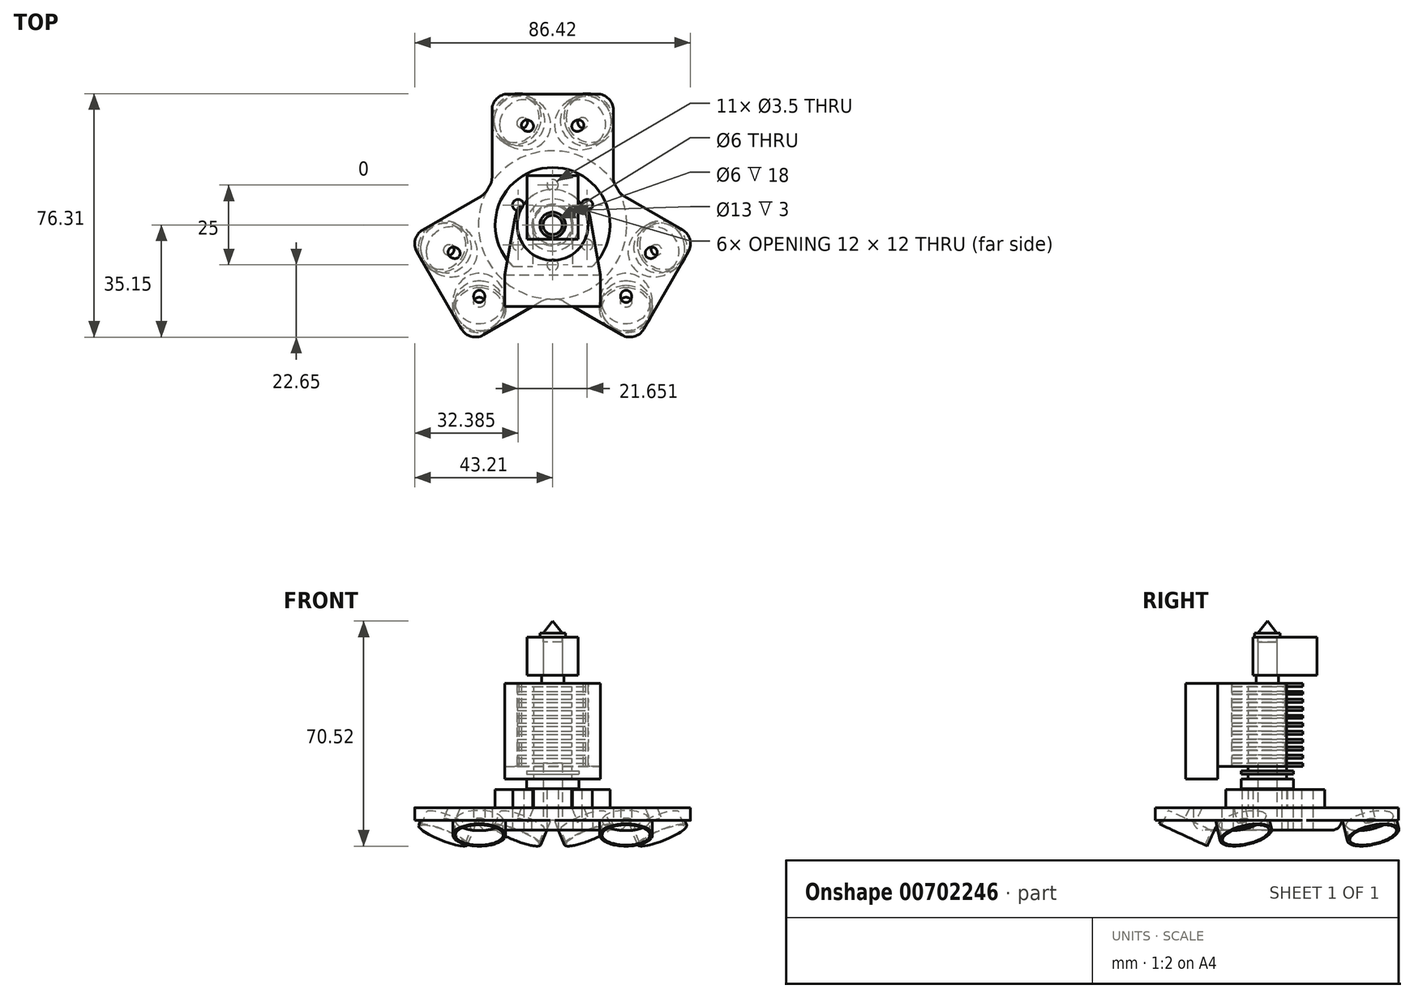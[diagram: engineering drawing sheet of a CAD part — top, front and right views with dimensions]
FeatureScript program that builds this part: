
annotation { "Feature Type Name" : "Feature", "Feature Type Description" : "" }
export const myFeature = defineFeature(function(context is Context, id is Id, definition is map)
    precondition{}
    {
        {
            var Q0;
            Q0=qCreatedBy(makeId("Top.planeOp"),FACE);
            var sketch = newSketch(context, id + "F0", { "sketchPlane" : qUnion([Q0])});
            skLineSegment(sketch, "E0", {"start": v(35.54, -20.52) * mm, "end": v(-20.14, 11.63) * mm, "construction": true});
            skLineSegment(sketch, "E1", {"start": v(0, 41.04) * mm, "end": v(0, -23.25) * mm, "construction": true});
            skLineSegment(sketch, "E2", {"start": v(-33.07, -19.1) * mm, "end": v(20.14, 11.62) * mm, "construction": true});
            skPoint(sketch, "E3", {"position": v(0, 0) * mm});
            skCircle(sketch, "E4", {"center": v(0, 0) * mm, "radius": 23.25 * mm});
            skPoint(sketch, "E5.visualSharp", {"position": v(-19, 41.04) * mm});
            skPoint(sketch, "E6.visualSharp", {"position": v(19, 41.04) * mm});
            skPoint(sketch, "E7.visualSharp", {"position": v(45.04, -4.07) * mm});
            skPoint(sketch, "E8.visualSharp", {"position": v(26.04, -36.98) * mm});
            skPoint(sketch, "E9.visualSharp", {"position": v(-26.04, -36.98) * mm});
            skPoint(sketch, "E10.visualSharp", {"position": v(-45.04, -4.07) * mm});
            skCircle(sketch, "E11", {"center": v(0, 0) * mm, "radius": 8 * mm});
            skCircle(sketch, "E12", {"center": v(0, 12.5) * mm, "radius": 1.75 * mm});
            skCircle(sketch, "E13", {"center": v(10.83, 6.25) * mm, "radius": 1.75 * mm});
            skCircle(sketch, "E14", {"center": v(10.83, -6.25) * mm, "radius": 1.75 * mm});
            skCircle(sketch, "E15", {"center": v(0, -12.5) * mm, "radius": 1.75 * mm});
            skCircle(sketch, "E16", {"center": v(-10.83, -6.25) * mm, "radius": 1.75 * mm});
            skCircle(sketch, "E17", {"center": v(-10.83, 6.25) * mm, "radius": 1.75 * mm});
            skCircle(sketch, "E18", {"center": v(0, 0) * mm, "radius": 6.5 * mm});
            skPoint(sketch, "E19.orphan", {"position": v(-21.1, 9.75) * mm});
            skPoint(sketch, "E20.orphan", {"position": v(-19, 13.4) * mm});
            skPoint(sketch, "E21.orphan", {"position": v(19, 13.4) * mm});
            skPoint(sketch, "E22.orphan", {"position": v(21.1, 9.75) * mm});
            skPoint(sketch, "E23.orphan", {"position": v(-2.1, -23.15) * mm});
            skPoint(sketch, "E24.orphan", {"position": v(2.1, -23.15) * mm});
            skLineSegment(sketch, "E25", {"start": v(32.5, -7.8) * mm, "end": v(23, -24.25) * mm, "construction": true});
            skLineSegment(sketch, "E26", {"start": v(-23, -24.25) * mm, "end": v(-32.5, -7.8) * mm, "construction": true});
            skLineSegment(sketch, "E27", {"start": v(-9.5, 32.04) * mm, "end": v(9.5, 32.04) * mm, "construction": true});
            skLineSegment(sketch, "E28", {"start": v(23, -24.25) * mm, "end": v(-23, -24.25) * mm, "construction": true});
            skCircle(sketch, "E29", {"center": v(0, 0) * mm, "radius": 12.5 * mm});
            skLineSegment(sketch, "E30", {"start": v(19, 41.04) * mm, "end": v(19, 13.4) * mm});
            skLineSegment(sketch, "E31", {"start": v(-19, 41.04) * mm, "end": v(-19, 13.4) * mm});
            skLineSegment(sketch, "E32", {"start": v(-21.1, 9.75) * mm, "end": v(-45.04, -4.07) * mm});
            skLineSegment(sketch, "E33", {"start": v(-2.1, -23.15) * mm, "end": v(-26.04, -36.98) * mm});
            skLineSegment(sketch, "E34", {"start": v(2.1, -23.15) * mm, "end": v(26.04, -36.98) * mm});
            skLineSegment(sketch, "E35", {"start": v(45.04, -4.07) * mm, "end": v(21.1, 9.75) * mm});
            skLineSegment(sketch, "E36", {"start": v(45.04, -4.07) * mm, "end": v(26.04, -36.98) * mm});
            skLineSegment(sketch, "E37", {"start": v(-26.04, -36.98) * mm, "end": v(-45.04, -4.07) * mm});
            skLineSegment(sketch, "E38", {"start": v(19, 41.04) * mm, "end": v(-19, 41.04) * mm});
            skLineSegment(sketch, "E39", {"start": v(-9.5, 32.04) * mm, "end": v(-32.5, -7.8) * mm, "construction": true});
            skLineSegment(sketch, "E40", {"start": v(9.5, 32.04) * mm, "end": v(32.5, -7.8) * mm, "construction": true});
            skSolve(sketch);
        }
        {
            var Q0;
            {var subQ0=sQuery(id+"F0.wireOp",EDGE,"E4");var subQ1=sQuery(id+"F0.wireOp",EDGE,"E0");var subQ2=makeQuery(id+"F0.imprint","INTERSECT",VERTEX,{"disambiguationData":[OD(0.0)],"derivedFrom":[subQ1,subQ0]});Q0=makeQuery(id+"F0.imprint","IMPRINT",FACE,{"disambiguationData":[TD([[makeQuery(id+"F0.imprint","IMPRINT",EDGE,{"disambiguationData":[TD([[subQ2,1.0]])],"derivedFrom":subQ1}),-1.0]])]});}
            var Q1;
            {var subQ0=sQuery(id+"F0.wireOp",EDGE,"E4");var subQ6=sQuery(id+"F0.wireOp",EDGE,"E1");var subQ7=makeQuery(id+"F0.imprint","INTERSECT",VERTEX,{"disambiguationData":[OD(1.0)],"derivedFrom":[subQ6,subQ0]});Q1=makeQuery(id+"F0.imprint","IMPRINT",FACE,{"disambiguationData":[TD([[makeQuery(id+"F0.imprint","IMPRINT",EDGE,{"disambiguationData":[TD([[subQ7,-1.0]])],"derivedFrom":subQ6}),1.0]])]});}
            var Q2;
            {var subQ0=sQuery(id+"F0.wireOp",EDGE,"E4");var subQ4=sQuery(id+"F0.wireOp",EDGE,"E0");var subQ5=makeQuery(id+"F0.imprint","INTERSECT",VERTEX,{"disambiguationData":[OD(1.0)],"derivedFrom":[subQ4,subQ0]});Q2=makeQuery(id+"F0.imprint","IMPRINT",FACE,{"disambiguationData":[TD([[makeQuery(id+"F0.imprint","IMPRINT",EDGE,{"disambiguationData":[TD([[subQ5,-1.0]])],"derivedFrom":subQ4}),1.0]])]});}
            var Q3;
            {var subQ0=sQuery(id+"F0.wireOp",EDGE,"E4");var subQ1=sQuery(id+"F0.wireOp",EDGE,"E1");var subQ2=makeQuery(id+"F0.imprint","INTERSECT",VERTEX,{"disambiguationData":[OD(0.0)],"derivedFrom":[subQ1,subQ0]});Q3=makeQuery(id+"F0.imprint","IMPRINT",FACE,{"disambiguationData":[TD([[makeQuery(id+"F0.imprint","IMPRINT",EDGE,{"disambiguationData":[TD([[subQ2,1.0]])],"derivedFrom":subQ1}),-1.0]])]});}
            var Q4;
            {var subQ0=sQuery(id+"F0.wireOp",EDGE,"E4");var subQ6=sQuery(id+"F0.wireOp",EDGE,"E0");var subQ7=makeQuery(id+"F0.imprint","INTERSECT",VERTEX,{"disambiguationData":[OD(0.0)],"derivedFrom":[subQ6,subQ0]});Q4=makeQuery(id+"F0.imprint","IMPRINT",FACE,{"disambiguationData":[TD([[makeQuery(id+"F0.imprint","IMPRINT",EDGE,{"disambiguationData":[TD([[subQ7,1.0]])],"derivedFrom":subQ6}),1.0]])]});}
            var Q5;
            {var subQ0=sQuery(id+"F0.wireOp",EDGE,"E4");var subQ2=sQuery(id+"F0.wireOp",EDGE,"E0");var subQ3=makeQuery(id+"F0.imprint","INTERSECT",VERTEX,{"disambiguationData":[OD(1.0)],"derivedFrom":[subQ2,subQ0]});Q5=makeQuery(id+"F0.imprint","IMPRINT",FACE,{"disambiguationData":[TD([[makeQuery(id+"F0.imprint","IMPRINT",EDGE,{"disambiguationData":[TD([[subQ3,-1.0]])],"derivedFrom":subQ2}),-1.0]])]});}
            var Q6;
            {var subQ0=sQuery(id+"F0.wireOp",EDGE,"qkuUuL0Q-UyTH-8MkL-LkHn-57lLYN8WkIcS");Q6=makeQuery(id+"F0.imprint","IMPRINT",FACE,{"disambiguationData":[TD([[makeQuery(id+"F0.imprint","IMPRINT",EDGE,{"derivedFrom":subQ0}),1.0]])]});}
            var Q7;
            {var subQ0=sQuery(id+"F0.wireOp",EDGE,"6XMY1UJf-UM1e-wrGH-O6Nx-o6CUiSNOfF3h");Q7=makeQuery(id+"F0.imprint","IMPRINT",FACE,{"disambiguationData":[TD([[makeQuery(id+"F0.imprint","IMPRINT",EDGE,{"derivedFrom":subQ0}),-1.0]])]});}
            var Q8;
            {var subQ0=sQuery(id+"F0.wireOp",EDGE,"eukLZOu2-N7H3-R9jE-bvm5-4IVGkD4qmDMb");Q8=makeQuery(id+"F0.imprint","IMPRINT",FACE,{"disambiguationData":[TD([[makeQuery(id+"F0.imprint","IMPRINT",EDGE,{"derivedFrom":subQ0}),1.0]])]});}
            var Q9;
            {var subQ0=sQuery(id+"F0.wireOp",EDGE,"v7Y52Qwb-cpJT-GfTj-oTL0-BVczpkMSaDcX");Q9=makeQuery(id+"F0.imprint","IMPRINT",FACE,{"disambiguationData":[TD([[makeQuery(id+"F0.imprint","IMPRINT",EDGE,{"derivedFrom":subQ0}),-1.0]])]});}
            var Q10;
            {var subQ0=sQuery(id+"F0.wireOp",EDGE,"TscbFwqg-n3GG-JwWl-lvQm-5aTHTKTKryP0");Q10=makeQuery(id+"F0.imprint","IMPRINT",FACE,{"disambiguationData":[TD([[makeQuery(id+"F0.imprint","IMPRINT",EDGE,{"derivedFrom":subQ0}),1.0]])]});}
            var Q11;
            {var subQ0=sQuery(id+"F0.wireOp",EDGE,"fuk3oV6k-3Qym-JvgU-Z5Bd-90OQX8uVS8cI");Q11=makeQuery(id+"F0.imprint","IMPRINT",FACE,{"disambiguationData":[TD([[makeQuery(id+"F0.imprint","IMPRINT",EDGE,{"derivedFrom":subQ0}),-1.0]])]});}
            var Q12;
            {var subQ7=sQuery(id+"F0.wireOp",EDGE,"E11");var subQ9=sQuery(id+"F0.wireOp",EDGE,"E0");var subQ10=makeQuery(id+"F0.imprint","INTERSECT",VERTEX,{"disambiguationData":[OD(1.0)],"derivedFrom":[subQ9,subQ7]});Q12=makeQuery(id+"F0.imprint","IMPRINT",FACE,{"disambiguationData":[TD([[makeQuery(id+"F0.imprint","IMPRINT",EDGE,{"disambiguationData":[TD([[subQ10,-1.0]])],"derivedFrom":subQ9}),-1.0]])]});}
            var Q13;
            {var subQ3=sQuery(id+"F0.wireOp",EDGE,"E12");var subQ6=sQuery(id+"F0.wireOp",EDGE,"E1");var subQ11=makeQuery(id+"F0.imprint","INTERSECT",VERTEX,{"disambiguationData":[OD(1.0)],"derivedFrom":[subQ6,subQ3]});Q13=makeQuery(id+"F0.imprint","IMPRINT",FACE,{"disambiguationData":[TD([[makeQuery(id+"F0.imprint","IMPRINT",EDGE,{"disambiguationData":[TD([[subQ11,-1.0]])],"derivedFrom":subQ6}),1.0]])]});}
            var Q14;
            {var subQ3=sQuery(id+"F0.wireOp",EDGE,"E14");var subQ5=sQuery(id+"F0.wireOp",EDGE,"E0");var subQ6=makeQuery(id+"F0.imprint","INTERSECT",VERTEX,{"disambiguationData":[OD(1.0)],"derivedFrom":[subQ5,subQ3]});Q14=makeQuery(id+"F0.imprint","IMPRINT",FACE,{"disambiguationData":[TD([[makeQuery(id+"F0.imprint","IMPRINT",EDGE,{"disambiguationData":[TD([[subQ6,-1.0]])],"derivedFrom":subQ5}),-1.0]])]});}
            var Q15;
            {var subQ1=sQuery(id+"F0.wireOp",EDGE,"E0");var subQ9=sQuery(id+"F0.wireOp",EDGE,"E14");var subQ11=makeQuery(id+"F0.imprint","INTERSECT",VERTEX,{"disambiguationData":[OD(1.0)],"derivedFrom":[subQ1,subQ9]});Q15=makeQuery(id+"F0.imprint","IMPRINT",FACE,{"disambiguationData":[TD([[makeQuery(id+"F0.imprint","IMPRINT",EDGE,{"disambiguationData":[TD([[subQ11,-1.0]])],"derivedFrom":subQ1}),1.0]])]});}
            var Q16;
            {var subQ0=sQuery(id+"F0.wireOp",EDGE,"E11");var subQ1=sQuery(id+"F0.wireOp",EDGE,"E1");var subQ2=makeQuery(id+"F0.imprint","INTERSECT",VERTEX,{"disambiguationData":[OD(1.0)],"derivedFrom":[subQ1,subQ0]});Q16=makeQuery(id+"F0.imprint","IMPRINT",FACE,{"disambiguationData":[TD([[makeQuery(id+"F0.imprint","IMPRINT",EDGE,{"disambiguationData":[TD([[subQ2,-1.0]])],"derivedFrom":subQ1}),-1.0]])]});}
            var Q17;
            {var subQ5=sQuery(id+"F0.wireOp",EDGE,"E11");var subQ6=sQuery(id+"F0.wireOp",EDGE,"E0");var subQ7=makeQuery(id+"F0.imprint","INTERSECT",VERTEX,{"disambiguationData":[OD(1.0)],"derivedFrom":[subQ6,subQ5]});Q17=makeQuery(id+"F0.imprint","IMPRINT",FACE,{"disambiguationData":[TD([[makeQuery(id+"F0.imprint","IMPRINT",EDGE,{"disambiguationData":[TD([[subQ7,-1.0]])],"derivedFrom":subQ6}),1.0]])]});}
            var Q18;
            {var subQ0=sQuery(id+"F0.wireOp",EDGE,"E4");var subQ4=sQuery(id+"F0.wireOp",EDGE,"E1");var subQ5=makeQuery(id+"F0.imprint","INTERSECT",VERTEX,{"derivedFrom":[subQ4,subQ0]});Q18=makeQuery(id+"F0.imprint","IMPRINT",FACE,{"disambiguationData":[TD([[makeQuery(id+"F0.imprint","IMPRINT",EDGE,{"disambiguationData":[TD([[subQ5,-1.0]])],"derivedFrom":subQ4}),-1.0]])]});}
            var Q19;
            {var subQ0=sQuery(id+"F0.wireOp",EDGE,"E4");var subQ4=sQuery(id+"F0.wireOp",EDGE,"E2");var subQ5=makeQuery(id+"F0.imprint","INTERSECT",VERTEX,{"derivedFrom":[subQ4,subQ0]});Q19=makeQuery(id+"F0.imprint","IMPRINT",FACE,{"disambiguationData":[TD([[makeQuery(id+"F0.imprint","IMPRINT",EDGE,{"disambiguationData":[TD([[subQ5,-1.0]])],"derivedFrom":subQ4}),-1.0]])]});}
            var Q20;
            {var subQ1=sQuery(id+"F0.wireOp",EDGE,"E4");var subQ3=sQuery(id+"F0.wireOp",EDGE,"eukLZOu2-N7H3-R9jE-bvm5-4IVGkD4qmDMb");var subQ4=makeQuery(id+"F0.imprint","INTERSECT",VERTEX,{"derivedFrom":[subQ1,subQ3]});Q20=makeQuery(id+"F0.imprint","IMPRINT",FACE,{"disambiguationData":[TD([[makeQuery(id+"F0.imprint","IMPRINT",EDGE,{"disambiguationData":[TD([[subQ4,1.0]])],"derivedFrom":subQ3}),-1.0]])]});}
            var Q21;
            {var subQ1=sQuery(id+"F0.wireOp",EDGE,"E4");var subQ3=sQuery(id+"F0.wireOp",EDGE,"6XMY1UJf-UM1e-wrGH-O6Nx-o6CUiSNOfF3h");var subQ4=makeQuery(id+"F0.imprint","INTERSECT",VERTEX,{"derivedFrom":[subQ1,subQ3]});Q21=makeQuery(id+"F0.imprint","IMPRINT",FACE,{"disambiguationData":[TD([[makeQuery(id+"F0.imprint","IMPRINT",EDGE,{"disambiguationData":[TD([[subQ4,1.0]])],"derivedFrom":subQ3}),1.0]])]});}
            var Q22;
            {var subQ1=sQuery(id+"F0.wireOp",EDGE,"E4");var subQ3=sQuery(id+"F0.wireOp",EDGE,"qkuUuL0Q-UyTH-8MkL-LkHn-57lLYN8WkIcS");var subQ4=makeQuery(id+"F0.imprint","INTERSECT",VERTEX,{"derivedFrom":[subQ1,subQ3]});Q22=makeQuery(id+"F0.imprint","IMPRINT",FACE,{"disambiguationData":[TD([[makeQuery(id+"F0.imprint","IMPRINT",EDGE,{"disambiguationData":[TD([[subQ4,1.0]])],"derivedFrom":subQ3}),-1.0]])]});}
            var Q23;
            {var subQ1=sQuery(id+"F0.wireOp",EDGE,"E4");var subQ3=sQuery(id+"F0.wireOp",EDGE,"fuk3oV6k-3Qym-JvgU-Z5Bd-90OQX8uVS8cI");var subQ4=makeQuery(id+"F0.imprint","INTERSECT",VERTEX,{"derivedFrom":[subQ1,subQ3]});Q23=makeQuery(id+"F0.imprint","IMPRINT",FACE,{"disambiguationData":[TD([[makeQuery(id+"F0.imprint","IMPRINT",EDGE,{"disambiguationData":[TD([[subQ4,1.0]])],"derivedFrom":subQ3}),1.0]])]});}
            var Q24;
            {var subQ1=sQuery(id+"F0.wireOp",EDGE,"E4");var subQ3=sQuery(id+"F0.wireOp",EDGE,"TscbFwqg-n3GG-JwWl-lvQm-5aTHTKTKryP0");var subQ4=makeQuery(id+"F0.imprint","INTERSECT",VERTEX,{"derivedFrom":[subQ1,subQ3]});Q24=makeQuery(id+"F0.imprint","IMPRINT",FACE,{"disambiguationData":[TD([[makeQuery(id+"F0.imprint","IMPRINT",EDGE,{"disambiguationData":[TD([[subQ4,1.0]])],"derivedFrom":subQ3}),-1.0]])]});}
            var Q25;
            {var subQ1=sQuery(id+"F0.wireOp",EDGE,"E4");var subQ3=sQuery(id+"F0.wireOp",EDGE,"v7Y52Qwb-cpJT-GfTj-oTL0-BVczpkMSaDcX");var subQ4=makeQuery(id+"F0.imprint","INTERSECT",VERTEX,{"derivedFrom":[subQ1,subQ3]});Q25=makeQuery(id+"F0.imprint","IMPRINT",FACE,{"disambiguationData":[TD([[makeQuery(id+"F0.imprint","IMPRINT",EDGE,{"disambiguationData":[TD([[subQ4,1.0]])],"derivedFrom":subQ3}),1.0]])]});}
            var Q26;
            {var subQ0=sQuery(id+"F0.wireOp",EDGE,"E4");var subQ4=sQuery(id+"F0.wireOp",EDGE,"E2");var subQ5=makeQuery(id+"F0.imprint","INTERSECT",VERTEX,{"derivedFrom":[subQ4,subQ0]});Q26=makeQuery(id+"F0.imprint","IMPRINT",FACE,{"disambiguationData":[TD([[makeQuery(id+"F0.imprint","IMPRINT",EDGE,{"disambiguationData":[TD([[subQ5,-1.0]])],"derivedFrom":subQ4}),1.0]])]});}
            var Q27;
            {var subQ0=sQuery(id+"F0.wireOp",EDGE,"E6.filletArc");Q27=makeQuery(id+"F0.imprint","IMPRINT",FACE,{"disambiguationData":[TD([[makeQuery(id+"F0.imprint","IMPRINT",EDGE,{"derivedFrom":subQ0}),1.0]])]});}
            var Q28;
            {var subQ0=sQuery(id+"F0.wireOp",EDGE,"E10.filletArc");Q28=makeQuery(id+"F0.imprint","IMPRINT",FACE,{"disambiguationData":[TD([[makeQuery(id+"F0.imprint","IMPRINT",EDGE,{"derivedFrom":subQ0}),1.0]])]});}
            var Q29;
            {var subQ0=sQuery(id+"F0.wireOp",EDGE,"E9.filletArc");Q29=makeQuery(id+"F0.imprint","IMPRINT",FACE,{"disambiguationData":[TD([[makeQuery(id+"F0.imprint","IMPRINT",EDGE,{"derivedFrom":subQ0}),1.0]])]});}
            var Q30;
            Q30=makeQuery(id+"F0.imprint","IMPRINT",FACE,{"disambiguationData":[TD([[makeQuery(id+"F0.imprint","IMPRINT",EDGE,{"derivedFrom":sQuery(id+"F0.wireOp",EDGE,"E11")}),-1.0]])]});
            var Q31;
            {var subQ9=sQuery(id+"F0.wireOp",EDGE,"E4");var subQ17=makeQuery(id+"F0.imprint","INTERSECT",VERTEX,{"derivedFrom":[subQ9,sQuery(id+"F0.wireOp",EDGE,"E30")]});Q31=makeQuery(id+"F0.imprint","IMPRINT",FACE,{"disambiguationData":[TD([[makeQuery(id+"F0.imprint","IMPRINT",EDGE,{"disambiguationData":[TD([[subQ17,1.0]])],"derivedFrom":subQ9}),1.0]])]});}
            var Q32;
            {var subQ0=sQuery(id+"F0.wireOp",EDGE,"E34");Q32=makeQuery(id+"F0.imprint","IMPRINT",FACE,{"disambiguationData":[TD([[makeQuery(id+"F0.imprint","IMPRINT",EDGE,{"derivedFrom":subQ0}),1.0]])]});}
            var Q33;
            {var subQ0=sQuery(id+"F0.wireOp",EDGE,"E30");Q33=makeQuery(id+"F0.imprint","IMPRINT",FACE,{"disambiguationData":[TD([[makeQuery(id+"F0.imprint","IMPRINT",EDGE,{"derivedFrom":subQ0}),-1.0]])]});}
            var Q34;
            {var subQ0=sQuery(id+"F0.wireOp",EDGE,"E32");Q34=makeQuery(id+"F0.imprint","IMPRINT",FACE,{"disambiguationData":[TD([[makeQuery(id+"F0.imprint","IMPRINT",EDGE,{"derivedFrom":subQ0}),1.0]])]});}
            extrude(context, id + "F1", {"entities" : qUnion([Q0, Q1, Q2, Q3, Q4, Q5, Q6, Q7, Q8, Q9, Q10, Q11, Q12, Q13, Q14, Q15, Q16, Q17, Q18, Q19, Q20, Q21, Q22, Q23, Q24, Q25, Q26, Q27, Q28, Q29, Q30, Q31, Q32, Q33, Q34]), "depth" : 4 * mm, "offsetDistance" : 25 * mm});
        }
        {
            var Q0;
            {var subQ9=sQuery(id+"F0.wireOp",EDGE,"E4");var subQ17=makeQuery(id+"F0.imprint","INTERSECT",VERTEX,{"derivedFrom":[subQ9,sQuery(id+"F0.wireOp",EDGE,"E30")]});Q0=makeQuery(id+"F0.imprint","IMPRINT",FACE,{"disambiguationData":[TD([[makeQuery(id+"F0.imprint","IMPRINT",EDGE,{"disambiguationData":[TD([[subQ17,1.0]])],"derivedFrom":subQ9}),1.0]])]});}
            var Q1;
            Q1=makeQuery(id+"F0.imprint","IMPRINT",FACE,{"disambiguationData":[TD([[makeQuery(id+"F0.imprint","IMPRINT",EDGE,{"derivedFrom":sQuery(id+"F0.wireOp",EDGE,"E11")}),-1.0]])]});
            var Q2;
            Q2=makeQuery(id+"F0.imprint","IMPRINT",FACE,{"disambiguationData":[TD([[makeQuery(id+"F0.imprint","IMPRINT",EDGE,{"derivedFrom":sQuery(id+"F0.wireOp",EDGE,"E11")}),1.0]])]});
            extrude(context, id + "F2", {"entities" : qUnion([Q0, Q1, Q2]), "operationType" : NewBodyOperationType.ADD, "oppositeDirection" : true, "depth" : 3 * mm, "offsetDistance" : 25 * mm});
        }
        {
            var Q0;
            Q0=sQuery(id+"F0.wireOp",EDGE,"E28");
            cPlane(context, id + "F3", {"entities" : qUnion([Q0]), "cplaneType" : CPlaneType.LINE_ANGLE, "offset" : 25 * mm, "angle" : 65 * degree, "oppositeDirection" : true, "width" : 150 * mm, "height" : 150 * mm});
        }
        {
            var Q0;
            Q0=qCreatedBy(id+"F3.planeOp",FACE);
            var sketch = newSketch(context, id + "F4", { "sketchPlane" : qUnion([Q0])});
            skLineSegment(sketch, "E41.0", {"start": v(23, 21.98) * mm, "end": v(-23, 21.98) * mm, "construction": true});
            skCircle(sketch, "E42", {"center": v(23, 21.98) * mm, "radius": 7.5 * mm});
            skCircle(sketch, "E43", {"center": v(-23, 21.98) * mm, "radius": 7.5 * mm});
            skCircle(sketch, "E44", {"center": v(23, 21.98) * mm, "radius": 8.25 * mm});
            skCircle(sketch, "E45", {"center": v(-23, 21.98) * mm, "radius": 8.25 * mm});
            skCircle(sketch, "E46", {"center": v(-23, 21.98) * mm, "radius": 1.75 * mm});
            skCircle(sketch, "E47", {"center": v(23, 21.98) * mm, "radius": 1.75 * mm});
            skSolve(sketch);
        }
        {
            var Q0;
            Q0=makeQuery(id+"F4.imprint","IMPRINT",FACE,{"disambiguationData":[TD([[makeQuery(id+"F4.imprint","IMPRINT",EDGE,{"derivedFrom":sQuery(id+"F4.wireOp",EDGE,"E42")}),-1.0]])]});
            var Q1;
            Q1=makeQuery(id+"F4.imprint","IMPRINT",FACE,{"disambiguationData":[TD([[makeQuery(id+"F4.imprint","IMPRINT",EDGE,{"derivedFrom":sQuery(id+"F4.wireOp",EDGE,"E42")}),1.0]])]});
            var Q2;
            Q2=makeQuery(id+"F4.imprint","IMPRINT",FACE,{"disambiguationData":[TD([[makeQuery(id+"F4.imprint","IMPRINT",EDGE,{"derivedFrom":sQuery(id+"F4.wireOp",EDGE,"E43")}),1.0]])]});
            var Q3;
            Q3=makeQuery(id+"F4.imprint","IMPRINT",FACE,{"disambiguationData":[TD([[makeQuery(id+"F4.imprint","IMPRINT",EDGE,{"derivedFrom":sQuery(id+"F4.wireOp",EDGE,"E43")}),-1.0]])]});
            var Q4;
            Q4=makeQuery(id+"F4.imprint","IMPRINT",FACE,{"disambiguationData":[TD([[makeQuery(id+"F4.imprint","IMPRINT",EDGE,{"derivedFrom":sQuery(id+"F4.wireOp",EDGE,"E47")}),1.0]])]});
            var Q5;
            Q5=makeQuery(id+"F4.imprint","IMPRINT",FACE,{"disambiguationData":[TD([[makeQuery(id+"F4.imprint","IMPRINT",EDGE,{"derivedFrom":sQuery(id+"F4.wireOp",EDGE,"E46")}),1.0]])]});
            extrude(context, id + "F5", {"entities" : qUnion([Q0, Q1, Q2, Q3, Q4, Q5]), "operationType" : NewBodyOperationType.ADD, "depth" : 5 * mm, "offsetDistance" : 25 * mm, "hasSecondDirection" : true, "secondDirectionOppositeDirection" : false, "secondDirectionDepth" : .5 * mm});
        }
        {
            var Q0;
            Q0=makeQuery(id+"F5.opExtrude","CAP_FACE",FACE,{"disambiguationData":[OSD([sQuery(id+"F4.wireOp",EDGE,"E45")])],"isStart":true});
            var Q1;
            Q1=makeQuery(id+"F5.opExtrude","CAP_FACE",FACE,{"disambiguationData":[OSD([sQuery(id+"F4.wireOp",EDGE,"E44")])],"isStart":true});
            var Q2;
            Q2=makeQuery(id+"F5.opExtrude","CAP_FACE",FACE,{"disambiguationData":[OSD([sQuery(id+"F4.wireOp",EDGE,"E44")])],"isStart":false});
            var Q3;
            Q3=makeQuery(id+"F5.opExtrude","CAP_FACE",FACE,{"disambiguationData":[OSD([sQuery(id+"F4.wireOp",EDGE,"E45")])],"isStart":false});
            extrude(context, id + "F6", {"entities" : qUnion([Q0, Q1, Q2, Q3]), "operationType" : NewBodyOperationType.ADD, "depth" : 4.4 * mm, "offsetDistance" : 25 * mm});
        }
        {
            var Q0;
            Q0=makeQuery(id+"F4.imprint","IMPRINT",FACE,{"disambiguationData":[TD([[makeQuery(id+"F4.imprint","IMPRINT",EDGE,{"derivedFrom":sQuery(id+"F4.wireOp",EDGE,"E43")}),1.0]])]});
            var Q1;
            Q1=makeQuery(id+"F4.imprint","IMPRINT",FACE,{"disambiguationData":[TD([[makeQuery(id+"F4.imprint","IMPRINT",EDGE,{"derivedFrom":sQuery(id+"F4.wireOp",EDGE,"E42")}),1.0]])]});
            extrude(context, id + "F7", {"entities" : qUnion([Q0, Q1]), "operationType" : NewBodyOperationType.REMOVE, "endBound" : BoundingType.THROUGH_ALL, "depth" : 5 * mm, "offsetDistance" : 25 * mm});
        }
        {
            var Q0;
            Q0=makeQuery(id+"F7.boolean.opBoolean","SPLIT",FACE,{"disambiguationData":[TD([makeQuery(id+"F7.opExtrude","SWEPT_FACE",FACE,{"disambiguationData":[OSD([sQuery(id+"F4.wireOp",EDGE,"E47")])]})])],"derivedFrom":makeQuery(id+"F5.opExtrude","CAP_FACE",FACE,{"disambiguationData":[OSD([sQuery(id+"F4.wireOp",EDGE,"E44")])],"isStart":false})});
            var Q1;
            Q1=makeQuery(id+"F7.boolean.opBoolean","SPLIT",FACE,{"disambiguationData":[TD([makeQuery(id+"F7.opExtrude","SWEPT_FACE",FACE,{"disambiguationData":[OSD([sQuery(id+"F4.wireOp",EDGE,"E46")])]})])],"derivedFrom":makeQuery(id+"F5.opExtrude","CAP_FACE",FACE,{"disambiguationData":[OSD([sQuery(id+"F4.wireOp",EDGE,"E45")])],"isStart":false})});
            extrude(context, id + "F8", {"entities" : qUnion([Q0, Q1]), "operationType" : NewBodyOperationType.REMOVE, "endBound" : BoundingType.THROUGH_ALL, "oppositeDirection" : true, "depth" : 25 * mm, "offsetDistance" : 25 * mm});
        }
        {
            var Q0;
            Q0=sQuery(id+"F0.wireOp",EDGE,"E39");
            cPlane(context, id + "F9", {"entities" : qUnion([Q0]), "cplaneType" : CPlaneType.LINE_ANGLE, "offset" : 25 * mm, "angle" : 25 * degree, "oppositeDirection" : true, "width" : 150 * mm, "height" : 150 * mm});
        }
        {
            var Q0;
            Q0=qCreatedBy(id+"F9.planeOp",FACE);
            var sketch = newSketch(context, id + "F10", { "sketchPlane" : qUnion([Q0])});
            skLineSegment(sketch, "E48.0", {"start": v(-6.18, -31.2) * mm, "end": v(-30.9, 7.6) * mm, "construction": true});
            skCircle(sketch, "E49", {"center": v(-30.9, 7.6) * mm, "radius": 7.5 * mm});
            skCircle(sketch, "E50", {"center": v(-30.9, 7.6) * mm, "radius": 8.25 * mm});
            skCircle(sketch, "E51", {"center": v(-30.9, 7.6) * mm, "radius": 1.75 * mm});
            skCircle(sketch, "E52", {"center": v(-6.18, -31.2) * mm, "radius": 7.5 * mm});
            skCircle(sketch, "E53", {"center": v(-6.18, -31.2) * mm, "radius": 8.25 * mm});
            skCircle(sketch, "E54", {"center": v(-6.18, -31.2) * mm, "radius": 1.75 * mm});
            skSolve(sketch);
        }
        {
            var Q0;
            Q0=makeQuery(id+"F10.imprint","IMPRINT",FACE,{"disambiguationData":[TD([[makeQuery(id+"F10.imprint","IMPRINT",EDGE,{"derivedFrom":sQuery(id+"F10.wireOp",EDGE,"E54")}),1.0]])]});
            var Q1;
            Q1=makeQuery(id+"F10.imprint","IMPRINT",FACE,{"disambiguationData":[TD([[makeQuery(id+"F10.imprint","IMPRINT",EDGE,{"derivedFrom":sQuery(id+"F10.wireOp",EDGE,"E52")}),1.0]])]});
            var Q2;
            Q2=makeQuery(id+"F10.imprint","IMPRINT",FACE,{"disambiguationData":[TD([[makeQuery(id+"F10.imprint","IMPRINT",EDGE,{"derivedFrom":sQuery(id+"F10.wireOp",EDGE,"E52")}),-1.0]])]});
            var Q3;
            Q3=makeQuery(id+"F10.imprint","IMPRINT",FACE,{"disambiguationData":[TD([[makeQuery(id+"F10.imprint","IMPRINT",EDGE,{"derivedFrom":sQuery(id+"F10.wireOp",EDGE,"E49")}),1.0]])]});
            var Q4;
            Q4=makeQuery(id+"F10.imprint","IMPRINT",FACE,{"disambiguationData":[TD([[makeQuery(id+"F10.imprint","IMPRINT",EDGE,{"derivedFrom":sQuery(id+"F10.wireOp",EDGE,"E51")}),1.0]])]});
            var Q5;
            Q5=makeQuery(id+"F10.imprint","IMPRINT",FACE,{"disambiguationData":[TD([[makeQuery(id+"F10.imprint","IMPRINT",EDGE,{"derivedFrom":sQuery(id+"F10.wireOp",EDGE,"E49")}),-1.0]])]});
            extrude(context, id + "F11", {"entities" : qUnion([Q0, Q1, Q2, Q3, Q4, Q5]), "operationType" : NewBodyOperationType.ADD, "depth" : 5 * mm, "offsetDistance" : 25 * mm, "hasSecondDirection" : true, "secondDirectionOppositeDirection" : true, "secondDirectionDepth" : .5 * mm});
        }
        {
            var Q0;
            Q0=makeQuery(id+"F11.opExtrude","CAP_FACE",FACE,{"disambiguationData":[OSD([sQuery(id+"F10.wireOp",EDGE,"E50")])],"isStart":true});
            var Q1;
            Q1=makeQuery(id+"F11.opExtrude","CAP_FACE",FACE,{"disambiguationData":[OSD([sQuery(id+"F10.wireOp",EDGE,"E53")])],"isStart":true});
            extrude(context, id + "F12", {"entities" : qUnion([Q0, Q1]), "operationType" : NewBodyOperationType.ADD, "depth" : 4.4 * mm, "offsetDistance" : 25 * mm});
        }
        {
            var Q0;
            Q0=makeQuery(id+"F10.imprint","IMPRINT",FACE,{"disambiguationData":[TD([[makeQuery(id+"F10.imprint","IMPRINT",EDGE,{"derivedFrom":sQuery(id+"F10.wireOp",EDGE,"E49")}),1.0]])]});
            var Q1;
            Q1=makeQuery(id+"F10.imprint","IMPRINT",FACE,{"disambiguationData":[TD([[makeQuery(id+"F10.imprint","IMPRINT",EDGE,{"derivedFrom":sQuery(id+"F10.wireOp",EDGE,"E52")}),1.0]])]});
            extrude(context, id + "F13", {"entities" : qUnion([Q0, Q1]), "operationType" : NewBodyOperationType.REMOVE, "endBound" : BoundingType.THROUGH_ALL, "depth" : 25 * mm, "offsetDistance" : 25 * mm});
        }
        {
            var Q0;
            Q0=makeQuery(id+"F13.boolean.opBoolean","SPLIT",FACE,{"disambiguationData":[TD([makeQuery(id+"F13.opExtrude","SWEPT_FACE",FACE,{"disambiguationData":[OSD([sQuery(id+"F10.wireOp",EDGE,"E51")])]})])],"derivedFrom":makeQuery(id+"F11.opExtrude","CAP_FACE",FACE,{"disambiguationData":[OSD([sQuery(id+"F10.wireOp",EDGE,"E50")])],"isStart":false})});
            var Q1;
            Q1=makeQuery(id+"F13.boolean.opBoolean","SPLIT",FACE,{"disambiguationData":[TD([makeQuery(id+"F13.opExtrude","SWEPT_FACE",FACE,{"disambiguationData":[OSD([sQuery(id+"F10.wireOp",EDGE,"E54")])]})])],"derivedFrom":makeQuery(id+"F11.opExtrude","CAP_FACE",FACE,{"disambiguationData":[OSD([sQuery(id+"F10.wireOp",EDGE,"E53")])],"isStart":false})});
            extrude(context, id + "F14", {"entities" : qUnion([Q0, Q1]), "operationType" : NewBodyOperationType.REMOVE, "endBound" : BoundingType.THROUGH_ALL, "oppositeDirection" : true, "depth" : 25 * mm, "offsetDistance" : 25 * mm});
        }
        {
            var Q0;
            Q0=makeQuery(id+"F1.opExtrude","SWEPT_EDGE",EDGE,{"disambiguationData":[OSD([sQuery(id+"F0.wireOp",EDGE,"E34"),sQuery(id+"F0.wireOp",EDGE,"E36")])]});
            var Q1;
            Q1=makeQuery(id+"F1.opExtrude","SWEPT_EDGE",EDGE,{"disambiguationData":[OSD([sQuery(id+"F0.wireOp",EDGE,"E33"),sQuery(id+"F0.wireOp",EDGE,"E37")])]});
            var Q2;
            Q2=makeQuery(id+"F1.opExtrude","SWEPT_EDGE",EDGE,{"disambiguationData":[OSD([sQuery(id+"F0.wireOp",EDGE,"E4"),sQuery(id+"F0.wireOp",EDGE,"E34")])]});
            var Q3;
            Q3=makeQuery(id+"F1.opExtrude","SWEPT_EDGE",EDGE,{"disambiguationData":[OSD([sQuery(id+"F0.wireOp",EDGE,"E4"),sQuery(id+"F0.wireOp",EDGE,"E33")])]});
            var Q4;
            Q4=makeQuery(id+"F1.opExtrude","SWEPT_EDGE",EDGE,{"disambiguationData":[OSD([sQuery(id+"F0.wireOp",EDGE,"E32"),sQuery(id+"F0.wireOp",EDGE,"E37")])]});
            var Q5;
            Q5=makeQuery(id+"F1.opExtrude","SWEPT_EDGE",EDGE,{"disambiguationData":[OSD([sQuery(id+"F0.wireOp",EDGE,"E4"),sQuery(id+"F0.wireOp",EDGE,"E32")])]});
            var Q6;
            Q6=makeQuery(id+"F1.opExtrude","SWEPT_EDGE",EDGE,{"disambiguationData":[OSD([sQuery(id+"F0.wireOp",EDGE,"E4"),sQuery(id+"F0.wireOp",EDGE,"E31")])]});
            var Q7;
            Q7=makeQuery(id+"F1.opExtrude","SWEPT_EDGE",EDGE,{"disambiguationData":[OSD([sQuery(id+"F0.wireOp",EDGE,"E31"),sQuery(id+"F0.wireOp",EDGE,"E38")])]});
            var Q8;
            Q8=makeQuery(id+"F1.opExtrude","SWEPT_EDGE",EDGE,{"disambiguationData":[OSD([sQuery(id+"F0.wireOp",EDGE,"E4"),sQuery(id+"F0.wireOp",EDGE,"E30")])]});
            var Q9;
            Q9=makeQuery(id+"F1.opExtrude","SWEPT_EDGE",EDGE,{"disambiguationData":[OSD([sQuery(id+"F0.wireOp",EDGE,"E30"),sQuery(id+"F0.wireOp",EDGE,"E38")])]});
            var Q10;
            Q10=makeQuery(id+"F1.opExtrude","SWEPT_EDGE",EDGE,{"disambiguationData":[OSD([sQuery(id+"F0.wireOp",EDGE,"E35"),sQuery(id+"F0.wireOp",EDGE,"E36")])]});
            var Q11;
            Q11=makeQuery(id+"F1.opExtrude","SWEPT_EDGE",EDGE,{"disambiguationData":[OSD([sQuery(id+"F0.wireOp",EDGE,"E4"),sQuery(id+"F0.wireOp",EDGE,"E35")])]});
            fillet(context, id + "F15", {"entities" : qUnion([Q0, Q1, Q2, Q3, Q4, Q5, Q6, Q7, Q8, Q9, Q10, Q11]), "radius" : 5 * mm, "tangentPropagation" : true, "allowEdgeOverflow" : false});
        }
        {
            var Q0;
            Q0=sQuery(id+"F0.wireOp",EDGE,"E40");
            cPlane(context, id + "F16", {"entities" : qUnion([Q0]), "cplaneType" : CPlaneType.LINE_ANGLE, "offset" : 25 * mm, "angle" : 25 * degree, "width" : 150 * mm, "height" : 150 * mm});
        }
        {
            var Q0;
            Q0=qCreatedBy(id+"F16.planeOp",FACE);
            var sketch = newSketch(context, id + "F17", { "sketchPlane" : qUnion([Q0])});
            skLineSegment(sketch, "E55.0", {"start": v(6.18, -31.2) * mm, "end": v(30.9, 7.6) * mm, "construction": true});
            skCircle(sketch, "E56", {"center": v(6.18, -31.2) * mm, "radius": 7.5 * mm});
            skCircle(sketch, "E57", {"center": v(30.9, 7.6) * mm, "radius": 7.5 * mm});
            skCircle(sketch, "E58", {"center": v(30.9, 7.6) * mm, "radius": 8.25 * mm});
            skCircle(sketch, "E59", {"center": v(6.18, -31.2) * mm, "radius": 8.25 * mm});
            skCircle(sketch, "E60", {"center": v(6.18, -31.2) * mm, "radius": 1.75 * mm});
            skCircle(sketch, "E61", {"center": v(30.9, 7.6) * mm, "radius": 1.75 * mm});
            skSolve(sketch);
        }
        {
            var Q0;
            Q0=makeQuery(id+"F17.imprint","IMPRINT",FACE,{"disambiguationData":[TD([[makeQuery(id+"F17.imprint","IMPRINT",EDGE,{"derivedFrom":sQuery(id+"F17.wireOp",EDGE,"E56")}),-1.0]])]});
            var Q1;
            Q1=makeQuery(id+"F17.imprint","IMPRINT",FACE,{"disambiguationData":[TD([[makeQuery(id+"F17.imprint","IMPRINT",EDGE,{"derivedFrom":sQuery(id+"F17.wireOp",EDGE,"E56")}),1.0]])]});
            var Q2;
            Q2=makeQuery(id+"F17.imprint","IMPRINT",FACE,{"disambiguationData":[TD([[makeQuery(id+"F17.imprint","IMPRINT",EDGE,{"derivedFrom":sQuery(id+"F17.wireOp",EDGE,"E60")}),1.0]])]});
            var Q3;
            Q3=makeQuery(id+"F17.imprint","IMPRINT",FACE,{"disambiguationData":[TD([[makeQuery(id+"F17.imprint","IMPRINT",EDGE,{"derivedFrom":sQuery(id+"F17.wireOp",EDGE,"E57")}),1.0]])]});
            var Q4;
            Q4=makeQuery(id+"F17.imprint","IMPRINT",FACE,{"disambiguationData":[TD([[makeQuery(id+"F17.imprint","IMPRINT",EDGE,{"derivedFrom":sQuery(id+"F17.wireOp",EDGE,"E57")}),-1.0]])]});
            var Q5;
            Q5=makeQuery(id+"F17.imprint","IMPRINT",FACE,{"disambiguationData":[TD([[makeQuery(id+"F17.imprint","IMPRINT",EDGE,{"derivedFrom":sQuery(id+"F17.wireOp",EDGE,"E61")}),1.0]])]});
            extrude(context, id + "F18", {"entities" : qUnion([Q0, Q1, Q2, Q3, Q4, Q5]), "operationType" : NewBodyOperationType.ADD, "depth" : 5 * mm, "offsetDistance" : 25 * mm, "hasSecondDirection" : true, "secondDirectionOppositeDirection" : true, "secondDirectionDepth" : .5 * mm});
        }
        {
            var Q0;
            Q0=makeQuery(id+"F18.opExtrude","CAP_FACE",FACE,{"disambiguationData":[OSD([sQuery(id+"F17.wireOp",EDGE,"E58")])],"isStart":true});
            var Q1;
            Q1=makeQuery(id+"F18.opExtrude","CAP_FACE",FACE,{"disambiguationData":[OSD([sQuery(id+"F17.wireOp",EDGE,"E59")])],"isStart":true});
            extrude(context, id + "F19", {"entities" : qUnion([Q0, Q1]), "operationType" : NewBodyOperationType.ADD, "depth" : 4.4 * mm, "offsetDistance" : 25 * mm});
        }
        {
            var Q0;
            Q0=makeQuery(id+"F17.imprint","IMPRINT",FACE,{"disambiguationData":[TD([[makeQuery(id+"F17.imprint","IMPRINT",EDGE,{"derivedFrom":sQuery(id+"F17.wireOp",EDGE,"E56")}),1.0]])]});
            var Q1;
            Q1=makeQuery(id+"F17.imprint","IMPRINT",FACE,{"disambiguationData":[TD([[makeQuery(id+"F17.imprint","IMPRINT",EDGE,{"derivedFrom":sQuery(id+"F17.wireOp",EDGE,"E57")}),1.0]])]});
            extrude(context, id + "F20", {"entities" : qUnion([Q0, Q1]), "operationType" : NewBodyOperationType.REMOVE, "endBound" : BoundingType.THROUGH_ALL, "depth" : 25 * mm, "offsetDistance" : 25 * mm});
        }
        {
            var Q0;
            Q0=makeQuery(id+"F20.boolean.opBoolean","SPLIT",FACE,{"disambiguationData":[TD([makeQuery(id+"F20.opExtrude","SWEPT_FACE",FACE,{"disambiguationData":[OSD([sQuery(id+"F17.wireOp",EDGE,"E60")])]})])],"derivedFrom":makeQuery(id+"F18.opExtrude","CAP_FACE",FACE,{"disambiguationData":[OSD([sQuery(id+"F17.wireOp",EDGE,"E59")])],"isStart":false})});
            var Q1;
            Q1=makeQuery(id+"F20.boolean.opBoolean","SPLIT",FACE,{"disambiguationData":[TD([makeQuery(id+"F20.opExtrude","SWEPT_FACE",FACE,{"disambiguationData":[OSD([sQuery(id+"F17.wireOp",EDGE,"E61")])]})])],"derivedFrom":makeQuery(id+"F18.opExtrude","CAP_FACE",FACE,{"disambiguationData":[OSD([sQuery(id+"F17.wireOp",EDGE,"E58")])],"isStart":false})});
            extrude(context, id + "F21", {"entities" : qUnion([Q0, Q1]), "operationType" : NewBodyOperationType.REMOVE, "endBound" : BoundingType.THROUGH_ALL, "oppositeDirection" : true, "depth" : 25 * mm, "offsetDistance" : 25 * mm});
        }
        {
            var Q0;
            Q0=makeQuery(id+"F2.opExtrude","CAP_EDGE",EDGE,{"disambiguationData":[OSD([sQuery(id+"F0.wireOp",EDGE,"E4")])],"isStart":false});
            fillet(context, id + "F22", {"entities" : qUnion([Q0]), "radius" : 3 * mm, "tangentPropagation" : true, "allowEdgeOverflow" : false});
        }
        {
            var Q0;
            Q0=makeQuery(id+"F0.imprint","IMPRINT",FACE,{"disambiguationData":[TD([[makeQuery(id+"F0.imprint","IMPRINT",EDGE,{"derivedFrom":sQuery(id+"F0.wireOp",EDGE,"E11")}),1.0]])]});
            var sketch = newSketch(context, id + "F23", { "sketchPlane" : qUnion([Q0])});
            skCircle(sketch, "E62.0", {"center": v(0, 0) * mm, "radius": 8 * mm});
            skCircle(sketch, "E63", {"center": v(0, 0) * mm, "radius": 6 * mm});
            skCircle(sketch, "E64", {"center": v(0, 0) * mm, "radius": 3 * mm});
            skSolve(sketch);
        }
        {
            var Q0;
            Q0=makeQuery(id+"F23.imprint","IMPRINT",FACE,{"disambiguationData":[TD([[makeQuery(id+"F23.imprint","IMPRINT",EDGE,{"derivedFrom":sQuery(id+"F23.wireOp",EDGE,"E63")}),1.0]])]});
            extrude(context, id + "F24", {"entities" : qUnion([Q0]), "depth" : 43 * mm, "offsetDistance" : 25 * mm});
        }
        {
            var Q0;
            Q0=qCreatedBy(makeId("Right.planeOp"),FACE);
            var sketch = newSketch(context, id + "F25", { "sketchPlane" : qUnion([Q0])});
            skLineSegment(sketch, "E65", {"start": v(3, 0) * mm, "end": v(8.17, 0) * mm});
            skLineSegment(sketch, "E66", {"start": v(8.17, 0) * mm, "end": v(8.17, 4) * mm});
            skLineSegment(sketch, "E67", {"start": v(8.17, 4) * mm, "end": v(3, 4) * mm});
            skLineSegment(sketch, "E68", {"start": v(3, 10) * mm, "end": v(8.17, 10) * mm});
            skLineSegment(sketch, "E69", {"start": v(8.17, 10) * mm, "end": v(8.17, 13) * mm});
            skLineSegment(sketch, "E70", {"start": v(8.17, 13) * mm, "end": v(3, 13) * mm});
            skLineSegment(sketch, "E71", {"start": v(3, 14.5) * mm, "end": v(8.17, 14.5) * mm});
            skLineSegment(sketch, "E72", {"start": v(8.17, 14.5) * mm, "end": v(8.17, 15.5) * mm});
            skLineSegment(sketch, "E73", {"start": v(8.17, 15.5) * mm, "end": v(3, 15.5) * mm});
            skLineSegment(sketch, "E74", {"start": v(3, 17) * mm, "end": v(11.1, 17) * mm});
            skLineSegment(sketch, "E75", {"start": v(11.1, 17) * mm, "end": v(11.1, 18) * mm});
            skLineSegment(sketch, "E76", {"start": v(11.1, 18) * mm, "end": v(3, 18) * mm});
            skLineSegment(sketch, "E77", {"start": v(3, 19.5) * mm, "end": v(11.1, 19.5) * mm});
            skLineSegment(sketch, "E78", {"start": v(11.1, 19.5) * mm, "end": v(11.1, 20.5) * mm});
            skLineSegment(sketch, "E79", {"start": v(11.1, 20.5) * mm, "end": v(3, 20.5) * mm});
            skLineSegment(sketch, "E80", {"start": v(3, 22) * mm, "end": v(11.1, 22) * mm});
            skLineSegment(sketch, "E81", {"start": v(11.1, 22) * mm, "end": v(11.1, 23) * mm});
            skLineSegment(sketch, "E82", {"start": v(11.1, 23) * mm, "end": v(3, 23) * mm});
            skLineSegment(sketch, "E83", {"start": v(3, 24.5) * mm, "end": v(11.1, 24.5) * mm});
            skLineSegment(sketch, "E84", {"start": v(11.1, 24.5) * mm, "end": v(11.1, 25.5) * mm});
            skLineSegment(sketch, "E85", {"start": v(11.1, 25.5) * mm, "end": v(3, 25.5) * mm});
            skLineSegment(sketch, "E86", {"start": v(3, 27) * mm, "end": v(11.1, 27) * mm});
            skLineSegment(sketch, "E87", {"start": v(11.1, 27) * mm, "end": v(11.1, 28) * mm});
            skLineSegment(sketch, "E88", {"start": v(11.1, 28) * mm, "end": v(3, 28) * mm});
            skLineSegment(sketch, "E89", {"start": v(3, 29.5) * mm, "end": v(11.1, 29.5) * mm});
            skLineSegment(sketch, "E90", {"start": v(11.1, 29.5) * mm, "end": v(11.1, 30.5) * mm});
            skLineSegment(sketch, "E91", {"start": v(11.1, 30.5) * mm, "end": v(3, 30.5) * mm});
            skLineSegment(sketch, "E92", {"start": v(3, 32) * mm, "end": v(11.1, 32) * mm});
            skLineSegment(sketch, "E93", {"start": v(11.1, 32) * mm, "end": v(11.1, 33) * mm});
            skLineSegment(sketch, "E94", {"start": v(11.1, 33) * mm, "end": v(3, 33) * mm});
            skLineSegment(sketch, "E95", {"start": v(3, 34.5) * mm, "end": v(11.1, 34.5) * mm});
            skLineSegment(sketch, "E96", {"start": v(11.1, 34.5) * mm, "end": v(11.1, 35.5) * mm});
            skLineSegment(sketch, "E97", {"start": v(11.1, 35.5) * mm, "end": v(3, 35.5) * mm});
            skLineSegment(sketch, "E98", {"start": v(3, 37) * mm, "end": v(11.1, 37) * mm});
            skLineSegment(sketch, "E99", {"start": v(11.1, 37) * mm, "end": v(11.1, 38) * mm});
            skLineSegment(sketch, "E100", {"start": v(11.1, 38) * mm, "end": v(3, 38) * mm});
            skLineSegment(sketch, "E101", {"start": v(3, 39.5) * mm, "end": v(11.1, 39.5) * mm});
            skLineSegment(sketch, "E102", {"start": v(11.1, 39.5) * mm, "end": v(11.1, 40.5) * mm});
            skLineSegment(sketch, "E103", {"start": v(11.1, 40.5) * mm, "end": v(3, 40.5) * mm});
            skLineSegment(sketch, "E104", {"start": v(3, 42) * mm, "end": v(11.1, 42) * mm});
            skLineSegment(sketch, "E105", {"start": v(11.1, 42) * mm, "end": v(11.1, 43) * mm});
            skLineSegment(sketch, "E106", {"start": v(11.1, 43) * mm, "end": v(3, 43) * mm});
            skLineSegment(sketch, "E107", {"start": v(3, 43) * mm, "end": v(3, 0) * mm});
            skLineSegment(sketch, "E108", {"start": v(0, 0) * mm, "end": v(0, 43) * mm});
            skSolve(sketch);
        }
        {
            var Q0;
            {var subQ0=sQuery(id+"F25.wireOp",EDGE,"E65");Q0=makeQuery(id+"F25.imprint","IMPRINT",FACE,{"disambiguationData":[TD([[makeQuery(id+"F25.imprint","IMPRINT",EDGE,{"derivedFrom":subQ0}),1.0]])]});}
            var Q1;
            {var subQ0=sQuery(id+"F25.wireOp",EDGE,"E68");Q1=makeQuery(id+"F25.imprint","IMPRINT",FACE,{"disambiguationData":[TD([[makeQuery(id+"F25.imprint","IMPRINT",EDGE,{"derivedFrom":subQ0}),1.0]])]});}
            var Q2;
            {var subQ0=sQuery(id+"F25.wireOp",EDGE,"E71");Q2=makeQuery(id+"F25.imprint","IMPRINT",FACE,{"disambiguationData":[TD([[makeQuery(id+"F25.imprint","IMPRINT",EDGE,{"derivedFrom":subQ0}),1.0]])]});}
            var Q3;
            {var subQ0=sQuery(id+"F25.wireOp",EDGE,"E74");Q3=makeQuery(id+"F25.imprint","IMPRINT",FACE,{"disambiguationData":[TD([[makeQuery(id+"F25.imprint","IMPRINT",EDGE,{"derivedFrom":subQ0}),1.0]])]});}
            var Q4;
            {var subQ0=sQuery(id+"F25.wireOp",EDGE,"E77");Q4=makeQuery(id+"F25.imprint","IMPRINT",FACE,{"disambiguationData":[TD([[makeQuery(id+"F25.imprint","IMPRINT",EDGE,{"derivedFrom":subQ0}),1.0]])]});}
            var Q5;
            {var subQ0=sQuery(id+"F25.wireOp",EDGE,"E80");Q5=makeQuery(id+"F25.imprint","IMPRINT",FACE,{"disambiguationData":[TD([[makeQuery(id+"F25.imprint","IMPRINT",EDGE,{"derivedFrom":subQ0}),1.0]])]});}
            var Q6;
            {var subQ0=sQuery(id+"F25.wireOp",EDGE,"E83");Q6=makeQuery(id+"F25.imprint","IMPRINT",FACE,{"disambiguationData":[TD([[makeQuery(id+"F25.imprint","IMPRINT",EDGE,{"derivedFrom":subQ0}),1.0]])]});}
            var Q7;
            {var subQ0=sQuery(id+"F25.wireOp",EDGE,"E86");Q7=makeQuery(id+"F25.imprint","IMPRINT",FACE,{"disambiguationData":[TD([[makeQuery(id+"F25.imprint","IMPRINT",EDGE,{"derivedFrom":subQ0}),1.0]])]});}
            var Q8;
            {var subQ0=sQuery(id+"F25.wireOp",EDGE,"E89");Q8=makeQuery(id+"F25.imprint","IMPRINT",FACE,{"disambiguationData":[TD([[makeQuery(id+"F25.imprint","IMPRINT",EDGE,{"derivedFrom":subQ0}),1.0]])]});}
            var Q9;
            {var subQ0=sQuery(id+"F25.wireOp",EDGE,"E92");Q9=makeQuery(id+"F25.imprint","IMPRINT",FACE,{"disambiguationData":[TD([[makeQuery(id+"F25.imprint","IMPRINT",EDGE,{"derivedFrom":subQ0}),1.0]])]});}
            var Q10;
            {var subQ0=sQuery(id+"F25.wireOp",EDGE,"E95");Q10=makeQuery(id+"F25.imprint","IMPRINT",FACE,{"disambiguationData":[TD([[makeQuery(id+"F25.imprint","IMPRINT",EDGE,{"derivedFrom":subQ0}),1.0]])]});}
            var Q11;
            {var subQ0=sQuery(id+"F25.wireOp",EDGE,"E98");Q11=makeQuery(id+"F25.imprint","IMPRINT",FACE,{"disambiguationData":[TD([[makeQuery(id+"F25.imprint","IMPRINT",EDGE,{"derivedFrom":subQ0}),1.0]])]});}
            var Q12;
            {var subQ0=sQuery(id+"F25.wireOp",EDGE,"E101");Q12=makeQuery(id+"F25.imprint","IMPRINT",FACE,{"disambiguationData":[TD([[makeQuery(id+"F25.imprint","IMPRINT",EDGE,{"derivedFrom":subQ0}),1.0]])]});}
            var Q13;
            {var subQ2=sQuery(id+"F25.wireOp",EDGE,"E104");Q13=makeQuery(id+"F25.imprint","IMPRINT",FACE,{"disambiguationData":[TD([[makeQuery(id+"F25.imprint","IMPRINT",EDGE,{"derivedFrom":subQ2}),1.0]])]});}
            var Q14;
            Q14=sQuery(id+"F25.wireOp",EDGE,"E108");
            revolve(context, id + "F26", {"operationType" : NewBodyOperationType.ADD, "surfaceOperationType" : NewSurfaceOperationType.NEW, "entities" : qUnion([Q0, Q1, Q2, Q3, Q4, Q5, Q6, Q7, Q8, Q9, Q10, Q11, Q12, Q13]), "axis" : qUnion([Q14]), "revolveType" : RevolveType.FULL});
        }
        {
            var Q0;
            Q0=makeQuery(id+"F26.boolean.opBoolean","MERGE",FACE,{"derivedFrom":[makeQuery(id+"F24.opExtrude","CAP_FACE",FACE,{"disambiguationData":[OSD([sQuery(id+"F23.wireOp",EDGE,"E63"),sQuery(id+"F23.wireOp",EDGE,"E64")])],"isStart":false}),makeQuery(id+"F26.opRevolve","SWEPT_FACE",FACE,{"disambiguationData":[OSD([sQuery(id+"F25.wireOp",EDGE,"E106")])]})]});
            var sketch = newSketch(context, id + "F27", { "sketchPlane" : qUnion([Q0])});
            skCircle(sketch, "E109.0", {"center": v(0, 0) * mm, "radius": 3 * mm});
            skCircle(sketch, "E110", {"center": v(0, 0) * mm, "radius": 3.5 * mm});
            skSolve(sketch);
        }
        {
            var Q0;
            Q0=makeQuery(id+"F27.imprint","IMPRINT",FACE,{"disambiguationData":[TD([[makeQuery(id+"F27.imprint","IMPRINT",EDGE,{"derivedFrom":sQuery(id+"F27.wireOp",EDGE,"E109.0")}),1.0]])]});
            extrude(context, id + "F28", {"entities" : qUnion([Q0]), "depth" : 13 * mm, "offsetDistance" : 25 * mm, "hasSecondDirection" : true, "secondDirectionOppositeDirection" : true, "secondDirectionDepth" : 25 * mm});
        }
        {
            var Q0;
            Q0=makeQuery(id+"F27.imprint","IMPRINT",FACE,{"disambiguationData":[TD([[makeQuery(id+"F27.imprint","IMPRINT",EDGE,{"derivedFrom":sQuery(id+"F27.wireOp",EDGE,"E109.0")}),-1.0]])]});
            extrude(context, id + "F29", {"entities" : qUnion([Q0]), "operationType" : NewBodyOperationType.ADD, "depth" : 2.5 * mm, "offsetDistance" : 25 * mm});
        }
        {
            var Q0;
            Q0=makeQuery(id+"F29.opExtrude","CAP_FACE",FACE,{"disambiguationData":[OSD([sQuery(id+"F27.wireOp",EDGE,"E109.0"),sQuery(id+"F27.wireOp",EDGE,"E110")])],"isStart":false});
            var sketch = newSketch(context, id + "F30", { "sketchPlane" : qUnion([Q0])});
            skCircle(sketch, "E111.0", {"center": v(0, 0) * mm, "radius": 3 * mm});
            skLineSegment(sketch, "E112.bottom", {"start": v(-8, -4.5) * mm, "end": v(8, -4.5) * mm});
            skLineSegment(sketch, "E112.top", {"start": v(-8, 15.5) * mm, "end": v(8, 15.5) * mm});
            skLineSegment(sketch, "E112.left", {"start": v(-8, -4.5) * mm, "end": v(-8, 15.5) * mm});
            skLineSegment(sketch, "E112.right", {"start": v(8, -4.5) * mm, "end": v(8, 15.5) * mm});
            skPoint(sketch, "E112.middle", {"position": v(0, 5.5) * mm});
            skSolve(sketch);
        }
        {
            var Q0;
            Q0=makeQuery(id+"F30.imprint","IMPRINT",FACE,{"disambiguationData":[TD([[makeQuery(id+"F30.imprint","IMPRINT",EDGE,{"derivedFrom":sQuery(id+"F30.wireOp",EDGE,"E112.bottom")}),1.0]])]});
            var Q1;
            Q1=makeQuery(id+"F30.imprint","IMPRINT",FACE,{"disambiguationData":[TD([[makeQuery(id+"F30.imprint","IMPRINT",EDGE,{"derivedFrom":sQuery(id+"F30.wireOp",EDGE,"E111.0")}),-1.0]])]});
            extrude(context, id + "F31", {"entities" : qUnion([Q0, Q1]), "depth" : 12 * mm, "offsetDistance" : 25 * mm});
        }
        {
            var Q0;
            Q0=qCreatedBy(makeId("Front.planeOp"),FACE);
            var sketch = newSketch(context, id + "F32", { "sketchPlane" : qUnion([Q0])});
            skLineSegment(sketch, "E113.0", {"start": v(-3, 56) * mm, "end": v(0, 56) * mm});
            skLineSegment(sketch, "E114.left", {"start": v(-3, 56) * mm, "end": v(-3, 57.5) * mm});
            skLineSegment(sketch, "E115", {"start": v(0, 62.5) * mm, "end": v(0, 56) * mm});
            skPoint(sketch, "E116.orphan", {"position": v(3, 56) * mm});
            skLineSegment(sketch, "E117", {"start": v(-3, 57.5) * mm, "end": v(-4, 57.5) * mm});
            skLineSegment(sketch, "E118", {"start": v(-3, 58.75) * mm, "end": v(0, 62.5) * mm});
            skLineSegment(sketch, "E119", {"start": v(-4, 57.5) * mm, "end": v(-4, 58.75) * mm});
            skLineSegment(sketch, "E120", {"start": v(-4, 58.75) * mm, "end": v(-3, 58.75) * mm});
            skSolve(sketch);
        }
        {
            var Q0;
            Q0=makeQuery(id+"F32.imprint","IMPRINT",FACE,{"disambiguationData":[TD([[makeQuery(id+"F32.imprint","IMPRINT",EDGE,{"derivedFrom":sQuery(id+"F32.wireOp",EDGE,"E113.0")}),1.0]])]});
            var Q1;
            Q1=sQuery(id+"F32.wireOp",EDGE,"E115");
            revolve(context, id + "F33", {"surfaceOperationType" : NewSurfaceOperationType.NEW, "entities" : qUnion([Q0]), "axis" : qUnion([Q1]), "revolveType" : RevolveType.FULL});
        }
        {
            var Q0;
            Q0=makeQuery(id+"F26.boolean.opBoolean","MERGE",FACE,{"derivedFrom":[makeQuery(id+"F24.opExtrude","CAP_FACE",FACE,{"disambiguationData":[OSD([sQuery(id+"F23.wireOp",EDGE,"E63"),sQuery(id+"F23.wireOp",EDGE,"E64")])],"isStart":false}),makeQuery(id+"F26.opRevolve","SWEPT_FACE",FACE,{"disambiguationData":[OSD([sQuery(id+"F25.wireOp",EDGE,"E106")])]})]});
            var sketch = newSketch(context, id + "F34", { "sketchPlane" : qUnion([Q0])});
            skCircle(sketch, "E121.0", {"center": v(0, 0) * mm, "radius": 11.1 * mm});
            skPoint(sketch, "E122", {"position": v(9.61, 5.55) * mm});
            skPoint(sketch, "E123", {"position": v(-9.61, 5.55) * mm});
            skLineSegment(sketch, "E124", {"start": v(0, 0) * mm, "end": v(9.61, 5.55) * mm});
            skLineSegment(sketch, "E125", {"start": v(0, 0) * mm, "end": v(-9.61, 5.55) * mm});
            skCircle(sketch, "E126", {"center": v(0, 0) * mm, "radius": 12 * mm});
            skLineSegment(sketch, "E127", {"start": v(9.61, 5.55) * mm, "end": v(10.4, 6) * mm});
            skLineSegment(sketch, "E128", {"start": v(-9.61, 5.55) * mm, "end": v(-10.4, 6) * mm});
            skLineSegment(sketch, "E129.bottom", {"start": v(-15, -15.6) * mm, "end": v(15, -15.6) * mm});
            skLineSegment(sketch, "E129.top", {"start": v(-15, -25.6) * mm, "end": v(15, -25.6) * mm});
            skLineSegment(sketch, "E129.left", {"start": v(-15, -15.6) * mm, "end": v(-15, -25.6) * mm});
            skLineSegment(sketch, "E129.right", {"start": v(15, -15.6) * mm, "end": v(15, -25.6) * mm});
            skPoint(sketch, "E129.middle", {"position": v(0, -20.6) * mm});
            skLineSegment(sketch, "E130", {"start": v(15, -15.6) * mm, "end": v(11.81, 2.13) * mm});
            skLineSegment(sketch, "E131", {"start": v(-15, -15.6) * mm, "end": v(-11.81, 2.13) * mm});
            skSolve(sketch);
        }
        {
            var Q0;
            Q0=makeQuery(id+"F34.imprint","IMPRINT",FACE,{"disambiguationData":[TD([[makeQuery(id+"F34.imprint","IMPRINT",EDGE,{"derivedFrom":sQuery(id+"F34.wireOp",EDGE,"E129.bottom")}),1.0]])]});
            var Q1;
            {var subQ4=sQuery(id+"F34.wireOp",EDGE,"E127");Q1=makeQuery(id+"F34.imprint","IMPRINT",FACE,{"disambiguationData":[TD([[makeQuery(id+"F34.imprint","IMPRINT",EDGE,{"derivedFrom":subQ4}),-1.0]])]});}
            extrude(context, id + "F35", {"entities" : qUnion([Q0, Q1]), "oppositeDirection" : true, "depth" : 26 * mm, "offsetDistance" : 25 * mm});
        }
        {
            var Q0;
            Q0=makeQuery(id+"F34.imprint","IMPRINT",FACE,{"disambiguationData":[TD([[makeQuery(id+"F34.imprint","IMPRINT",EDGE,{"derivedFrom":sQuery(id+"F34.wireOp",EDGE,"E129.bottom")}),-1.0]])]});
            extrude(context, id + "F36", {"entities" : qUnion([Q0]), "operationType" : NewBodyOperationType.ADD, "oppositeDirection" : true, "depth" : 30 * mm, "offsetDistance" : 25 * mm});
        }
        {
            var Q0;
            Q0=makeQuery(id+"F1.opExtrude","CAP_FACE",FACE,{"disambiguationData":[OSD([sQuery(id+"F0.wireOp",EDGE,"E4"),sQuery(id+"F0.wireOp",EDGE,"E11"),sQuery(id+"F0.wireOp",EDGE,"E12"),sQuery(id+"F0.wireOp",EDGE,"E13"),sQuery(id+"F0.wireOp",EDGE,"E14"),sQuery(id+"F0.wireOp",EDGE,"E15"),sQuery(id+"F0.wireOp",EDGE,"E16"),sQuery(id+"F0.wireOp",EDGE,"E17"),sQuery(id+"F0.wireOp",EDGE,"E30"),sQuery(id+"F0.wireOp",EDGE,"E31"),sQuery(id+"F0.wireOp",EDGE,"E32"),sQuery(id+"F0.wireOp",EDGE,"E33"),sQuery(id+"F0.wireOp",EDGE,"E34"),sQuery(id+"F0.wireOp",EDGE,"E35"),sQuery(id+"F0.wireOp",EDGE,"E36"),sQuery(id+"F0.wireOp",EDGE,"E37"),sQuery(id+"F0.wireOp",EDGE,"E38")])],"isStart":false});
            var sketch = newSketch(context, id + "F37", { "sketchPlane" : qUnion([Q0])});
            skArc(sketch, "E132", {"start": v(12.45, -13) * mm, "mid": v(0, 18) * mm, "end": v(-12.45, -13) * mm});
            skArc(sketch, "E133", {"start": v(6.25, 0) * mm, "mid": v(0, 6.25) * mm, "end": v(-6.25, 0) * mm});
            skCircle(sketch, "E134.0", {"center": v(10.83, 6.25) * mm, "radius": 1.75 * mm});
            skCircle(sketch, "E134.1", {"center": v(0, 12.5) * mm, "radius": 1.75 * mm});
            skCircle(sketch, "E134.2", {"center": v(-10.83, 6.25) * mm, "radius": 1.75 * mm});
            skCircle(sketch, "E134.3", {"center": v(-10.83, -6.25) * mm, "radius": 1.75 * mm});
            skCircle(sketch, "E134.5", {"center": v(10.83, -6.25) * mm, "radius": 1.75 * mm});
            skLineSegment(sketch, "E135", {"start": v(-6.25, 0) * mm, "end": v(-6.25, -13) * mm});
            skLineSegment(sketch, "E136", {"start": v(6.25, 0) * mm, "end": v(6.25, -13) * mm});
            skLineSegment(sketch, "E137", {"start": v(-12.45, -13) * mm, "end": v(-6.25, -13) * mm});
            skLineSegment(sketch, "E138.trimOffspring", {"start": v(6.25, -13) * mm, "end": v(12.45, -13) * mm});
            skSolve(sketch);
        }
        {
            var Q0;
            {var subQ0=sQuery(id+"F37.wireOp",EDGE,"E132");Q0=makeQuery(id+"F37.imprint","IMPRINT",FACE,{"disambiguationData":[TD([[makeQuery(id+"F37.imprint","IMPRINT",EDGE,{"derivedFrom":subQ0}),1.0]])]});}
            var Q1;
            {var subQ0=sQuery(id+"F37.wireOp",EDGE,"E133");Q1=makeQuery(id+"F37.imprint","IMPRINT",FACE,{"disambiguationData":[TD([[makeQuery(id+"F37.imprint","IMPRINT",EDGE,{"derivedFrom":subQ0}),-1.0]])]});}
            extrude(context, id + "F38", {"entities" : qUnion([Q0, Q1]), "depth" : 5.65 * mm, "offsetDistance" : 25 * mm});
        }
    });
